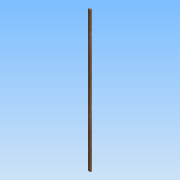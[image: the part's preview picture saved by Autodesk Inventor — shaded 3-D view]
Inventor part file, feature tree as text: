
AUTODESK INVENTOR PART (.ipt)
format: ipt  version: 2015 (Build 190159000, 159)  size: 84,480 bytes
history: native  units: mm
features: extrude x1, sketch x1
ambient origin geometry x8: Origin, YZ Plane, XZ Plane, XY Plane, X Axis, Y Axis, Z Axis, Center Point
bodies: Solid1 (feature_tree)
feature tree (2):
  extrude  "Extrusion1"  Depth=560.0mm
  sketch  "Sketch1"  dims[d0=5.0mm d1=0.0mm d2=560.0mm d3=20.0mm]
